# Revit family: 1299xxx Milo 300
name_source: partatom
category: Lighting Fixtures
units: mm (PartAtom-declared; Revit-internal decimal feet)

## family parameters
Always vertical = Yes
Cut with Voids When Loaded = No
Host = Wall
Light Source = No
OmniClass Number = 23.80.70.00
OmniClass Title = Lighting
Part Type = Normal
Room Calculation Point = No
Round Connector Dimension = Use Diameter
Shared = No

## types (2) — shared parameters
Driver Required = No
Main Material = Metal - Steel
Manufacturer = Astro Lighting Ltd
Manufacturer URL - Europe and Rest of World = www.astrolighting.com
Manufacturer URL - North America = us.astrolighting.com
Product CCT = 2700K / 3000K
Product CRI = 80 / 90
Product SKU = 1234001
URL = www.astrolighting.com
zero-valued in all types: Default Elevation, Electrical Class

## per-type parameters (varying)
| type | ADA compliant | Location / IP Rating | Product Location |
| CE | N / A |  |  |
| ETL |  | DAMP | Bathroom |

## geometry (parser evidence)
native form markers: Sweep x3
no freeform markers — native parametric forms only
